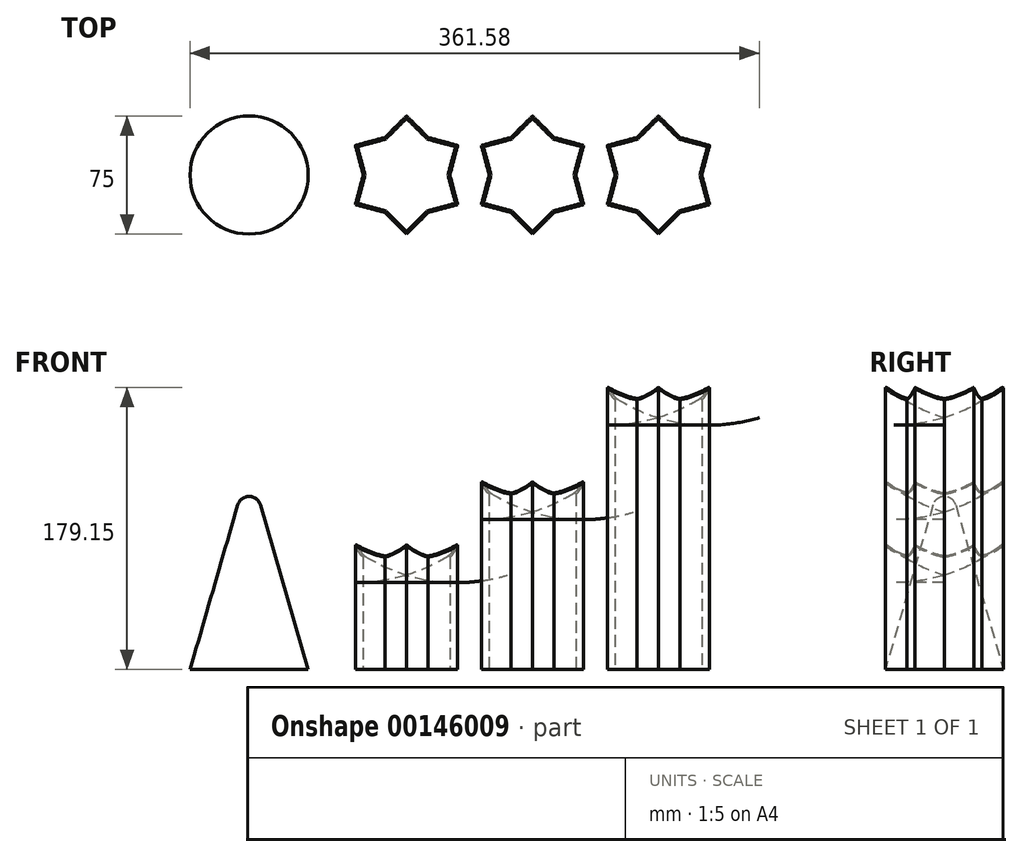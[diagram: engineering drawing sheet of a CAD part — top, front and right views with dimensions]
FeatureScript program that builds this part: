
annotation { "Feature Type Name" : "Feature", "Feature Type Description" : "" }
export const myFeature = defineFeature(function(context is Context, id is Id, definition is map)
    precondition{}
    {
        {
            var Q0;
            Q0=qCreatedBy(makeId("Front.planeOp"),FACE);
            var sketch = newSketch(context, id + "F0", { "sketchPlane" : qUnion([Q0])});
            skLineSegment(sketch, "E0", {"start": v(0, 0) * mm, "end": v(0, 110) * mm});
            skLineSegment(sketch, "E1", {"start": v(0, 0) * mm, "end": v(-37.5, 0) * mm});
            skLineSegment(sketch, "E2", {"start": v(-37.5, 0) * mm, "end": v(-7.2, 104.59) * mm});
            skArc(sketch, "E3", {"start": v(0, 110) * mm, "mid": v(-4.5, 108.5) * mm, "end": v(-7.2, 104.59) * mm});
            skLineSegment(sketch, "E4", {"start": v(0, 110) * mm, "end": v(-28.77, 110) * mm, "construction": true});
            skSolve(sketch);
        }
        {
            var Q0;
            Q0=makeQuery(id+"F0.imprint","IMPRINT",FACE,{"disambiguationData":[TD([[makeQuery(id+"F0.imprint","IMPRINT",EDGE,{"derivedFrom":sQuery(id+"F0.wireOp",EDGE,"E0")}),1.0]])]});
            var Q1;
            Q1=sQuery(id+"F0.wireOp",EDGE,"E0");
            revolve(context, id + "F1", {"entities" : qUnion([Q0]), "axis" : qUnion([Q1]), "revolveType" : RevolveType.FULL});
        }
        {
            var Q0;
            Q0=qCreatedBy(makeId("Top.planeOp"),FACE);
            var sketch = newSketch(context, id + "F2", { "sketchPlane" : qUnion([Q0])});
            skLineSegment(sketch, "E5", {"start": v(0, 0) * mm, "end": v(100, 0) * mm, "construction": true});
            skCircle(sketch, "E6", {"center": v(100, 0) * mm, "radius": 37.5 * mm, "construction": true});
            skLineSegment(sketch, "E7", {"start": v(72.5, 0) * mm, "end": v(67.52, 18.75) * mm});
            skLineSegment(sketch, "E8", {"start": v(67.52, 18.75) * mm, "end": v(86.25, 23.82) * mm});
            skLineSegment(sketch, "E9", {"start": v(86.25, 23.82) * mm, "end": v(100, 37.5) * mm});
            skLineSegment(sketch, "E10", {"start": v(100, 37.5) * mm, "end": v(113.75, 23.82) * mm});
            skLineSegment(sketch, "E11", {"start": v(113.75, 23.82) * mm, "end": v(132.48, 18.75) * mm});
            skLineSegment(sketch, "E12", {"start": v(132.48, 18.75) * mm, "end": v(127.5, 0) * mm});
            skCircle(sketch, "E13.0", {"center": v(100, 0) * mm, "radius": 27.5 * mm, "construction": true});
            skLineSegment(sketch, "E14.MirrorCS", {"start": v(72.5, 0) * mm, "end": v(67.52, -18.75) * mm});
            skLineSegment(sketch, "E15.MirrorCS", {"start": v(67.52, -18.75) * mm, "end": v(86.25, -23.82) * mm});
            skLineSegment(sketch, "E16.MirrorCS", {"start": v(86.25, -23.82) * mm, "end": v(100, -37.5) * mm});
            skLineSegment(sketch, "E17.MirrorCS", {"start": v(100, -37.5) * mm, "end": v(113.75, -23.82) * mm});
            skLineSegment(sketch, "E18.MirrorCS", {"start": v(113.75, -23.82) * mm, "end": v(132.48, -18.75) * mm});
            skLineSegment(sketch, "E19.MirrorCS", {"start": v(132.48, -18.75) * mm, "end": v(127.5, 0) * mm});
            skLineSegment(sketch, "E20.1.0.0", {"start": v(193.75, 23.82) * mm, "end": v(212.48, 18.75) * mm});
            skLineSegment(sketch, "E20.1.0.1", {"start": v(212.48, 18.75) * mm, "end": v(207.5, 0) * mm});
            skLineSegment(sketch, "E20.1.0.2", {"start": v(212.48, -18.75) * mm, "end": v(207.5, 0) * mm});
            skLineSegment(sketch, "E20.1.0.3", {"start": v(193.75, -23.82) * mm, "end": v(212.48, -18.75) * mm});
            skLineSegment(sketch, "E20.1.0.4", {"start": v(180, -37.5) * mm, "end": v(193.75, -23.82) * mm});
            skLineSegment(sketch, "E20.1.0.5", {"start": v(166.25, -23.82) * mm, "end": v(180, -37.5) * mm});
            skLineSegment(sketch, "E20.1.0.6", {"start": v(147.52, -18.75) * mm, "end": v(166.25, -23.82) * mm});
            skLineSegment(sketch, "E20.1.0.7", {"start": v(152.5, 0) * mm, "end": v(147.52, -18.75) * mm});
            skLineSegment(sketch, "E20.1.0.8", {"start": v(152.5, 0) * mm, "end": v(147.52, 18.75) * mm});
            skLineSegment(sketch, "E20.1.0.9", {"start": v(147.52, 18.75) * mm, "end": v(166.25, 23.82) * mm});
            skLineSegment(sketch, "E20.1.0.10", {"start": v(166.25, 23.82) * mm, "end": v(180, 37.5) * mm});
            skLineSegment(sketch, "E20.1.0.11", {"start": v(180, 37.5) * mm, "end": v(193.75, 23.82) * mm});
            skLineSegment(sketch, "E20.2.0.0", {"start": v(273.75, 23.82) * mm, "end": v(292.48, 18.75) * mm});
            skLineSegment(sketch, "E20.2.0.1", {"start": v(292.48, 18.75) * mm, "end": v(287.5, 0) * mm});
            skLineSegment(sketch, "E20.2.0.2", {"start": v(292.48, -18.75) * mm, "end": v(287.5, 0) * mm});
            skLineSegment(sketch, "E20.2.0.3", {"start": v(273.75, -23.82) * mm, "end": v(292.48, -18.75) * mm});
            skLineSegment(sketch, "E20.2.0.4", {"start": v(260, -37.5) * mm, "end": v(273.75, -23.82) * mm});
            skLineSegment(sketch, "E20.2.0.5", {"start": v(246.25, -23.82) * mm, "end": v(260, -37.5) * mm});
            skLineSegment(sketch, "E20.2.0.6", {"start": v(227.52, -18.75) * mm, "end": v(246.25, -23.82) * mm});
            skLineSegment(sketch, "E20.2.0.7", {"start": v(232.5, 0) * mm, "end": v(227.52, -18.75) * mm});
            skLineSegment(sketch, "E20.2.0.8", {"start": v(232.5, 0) * mm, "end": v(227.52, 18.75) * mm});
            skLineSegment(sketch, "E20.2.0.9", {"start": v(227.52, 18.75) * mm, "end": v(246.25, 23.82) * mm});
            skLineSegment(sketch, "E20.2.0.10", {"start": v(246.25, 23.82) * mm, "end": v(260, 37.5) * mm});
            skLineSegment(sketch, "E20.2.0.11", {"start": v(260, 37.5) * mm, "end": v(273.75, 23.82) * mm});
            skLineSegment(sketch, "E20.direction1", {"start": v(113.75, 23.82) * mm, "end": v(193.75, 23.82) * mm, "construction": true});
            skSolve(sketch);
        }
        {
            var Q0;
            Q0=makeQuery(id+"F2.imprint","IMPRINT",FACE,{"disambiguationData":[TD([[makeQuery(id+"F2.imprint","IMPRINT",EDGE,{"derivedFrom":sQuery(id+"F2.wireOp",EDGE,"E7")}),-1.0]])]});
            extrude(context, id + "F3", {"entities" : qUnion([Q0]), "depth" : 80 * mm});
        }
        {
            var Q0;
            Q0=makeQuery(id+"F2.imprint","IMPRINT",FACE,{"disambiguationData":[TD([[makeQuery(id+"F2.imprint","IMPRINT",EDGE,{"derivedFrom":sQuery(id+"F2.wireOp",EDGE,"E20.1.0.0")}),-1.0]])]});
            extrude(context, id + "F4", {"entities" : qUnion([Q0]), "depth" : 120 * mm});
        }
        {
            var Q0;
            Q0=makeQuery(id+"F2.imprint","IMPRINT",FACE,{"disambiguationData":[TD([[makeQuery(id+"F2.imprint","IMPRINT",EDGE,{"derivedFrom":sQuery(id+"F2.wireOp",EDGE,"E20.2.0.0")}),-1.0]])]});
            extrude(context, id + "F5", {"entities" : qUnion([Q0]), "depth" : 180 * mm});
        }
        {
            var Q0;
            Q0=qCreatedBy(makeId("Front.planeOp"),FACE);
            var sketch = newSketch(context, id + "F6", { "sketchPlane" : qUnion([Q0])});
            skLineSegment(sketch, "E21", {"start": v(100, 60) * mm, "end": v(100, 80) * mm});
            skLineSegment(sketch, "E22", {"start": v(180, 100) * mm, "end": v(180, 120) * mm});
            skLineSegment(sketch, "E23", {"start": v(260, 160) * mm, "end": v(260, 180) * mm});
            skArc(sketch, "E24", {"start": v(62.5, 80) * mm, "mid": v(80.27, 68.17) * mm, "end": v(100, 60) * mm});
            skLineSegment(sketch, "E25", {"start": v(62.5, 80) * mm, "end": v(100, 80) * mm});
            skLineSegment(sketch, "E26", {"start": v(180, 120) * mm, "end": v(142.5, 120) * mm});
            skLineSegment(sketch, "E27", {"start": v(260, 180) * mm, "end": v(222.5, 180) * mm});
            skArc(sketch, "E28", {"start": v(142.5, 120) * mm, "mid": v(160.27, 108.17) * mm, "end": v(180, 100) * mm});
            skArc(sketch, "E29", {"start": v(222.5, 180) * mm, "mid": v(240.27, 168.17) * mm, "end": v(260, 160) * mm});
            skSolve(sketch);
        }
        {
            var Q0;
            Q0=makeQuery(id+"F6.imprint","IMPRINT",FACE,{"disambiguationData":[TD([[makeQuery(id+"F6.imprint","IMPRINT",EDGE,{"derivedFrom":sQuery(id+"F6.wireOp",EDGE,"E21")}),1.0]])]});
            var Q1;
            Q1=sQuery(id+"F6.wireOp",EDGE,"E21");
            revolve(context, id + "F7", {"operationType" : NewBodyOperationType.REMOVE, "entities" : qUnion([Q0]), "axis" : qUnion([Q1]), "revolveType" : RevolveType.FULL, "oppositeDirection" : true});
        }
        {
            var Q0;
            Q0=makeQuery(id+"F6.imprint","IMPRINT",FACE,{"disambiguationData":[TD([[makeQuery(id+"F6.imprint","IMPRINT",EDGE,{"derivedFrom":sQuery(id+"F6.wireOp",EDGE,"E22")}),1.0]])]});
            var Q1;
            Q1=sQuery(id+"F6.wireOp",EDGE,"E22");
            revolve(context, id + "F8", {"operationType" : NewBodyOperationType.REMOVE, "entities" : qUnion([Q0]), "axis" : qUnion([Q1]), "revolveType" : RevolveType.FULL, "oppositeDirection" : true});
        }
        {
            var Q0;
            Q0=makeQuery(id+"F6.imprint","IMPRINT",FACE,{"disambiguationData":[TD([[makeQuery(id+"F6.imprint","IMPRINT",EDGE,{"derivedFrom":sQuery(id+"F6.wireOp",EDGE,"E23")}),1.0]])]});
            var Q1;
            Q1=sQuery(id+"F6.wireOp",EDGE,"E23");
            revolve(context, id + "F9", {"operationType" : NewBodyOperationType.REMOVE, "entities" : qUnion([Q0]), "axis" : qUnion([Q1]), "revolveType" : RevolveType.FULL, "oppositeDirection" : true});
        }
        {
            var Q0;
            Q0=makeQuery(id+"F7.boolean.opBoolean","COPY",FACE,{"derivedFrom":makeQuery(id+"F7.opRevolve","SWEPT_FACE",FACE,{"disambiguationData":[OSD([sQuery(id+"F6.wireOp",EDGE,"E24")])]})});
            var Q1;
            Q1=makeQuery(id+"F8.boolean.opBoolean","COPY",FACE,{"derivedFrom":makeQuery(id+"F8.opRevolve","SWEPT_FACE",FACE,{"disambiguationData":[OSD([sQuery(id+"F6.wireOp",EDGE,"E28")])]})});
            var Q2;
            Q2=makeQuery(id+"F9.boolean.opBoolean","COPY",FACE,{"derivedFrom":makeQuery(id+"F9.opRevolve","SWEPT_FACE",FACE,{"disambiguationData":[OSD([sQuery(id+"F6.wireOp",EDGE,"E29")])]})});
            fillet(context, id + "F10", {"entities" : qUnion([Q0, Q1, Q2]), "radius" : .75 * mm, "tangentPropagation" : true, "allowEdgeOverflow" : false});
        }
    });
